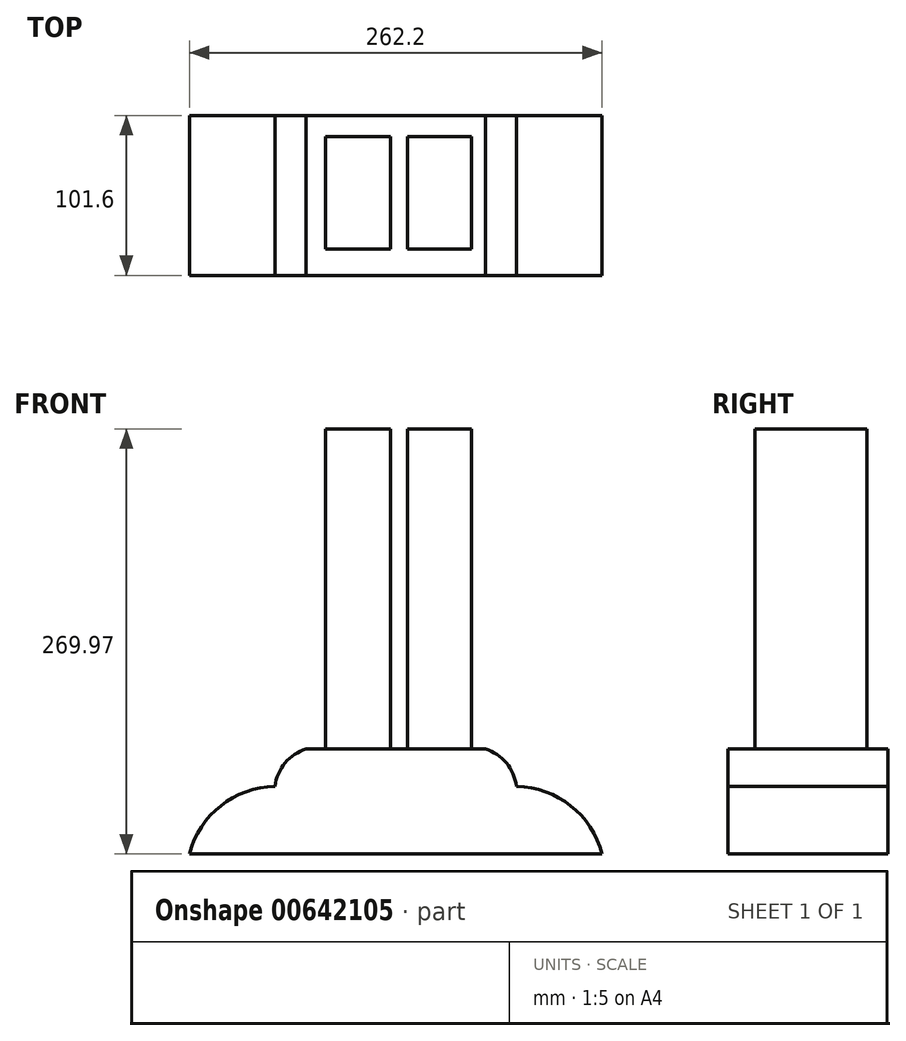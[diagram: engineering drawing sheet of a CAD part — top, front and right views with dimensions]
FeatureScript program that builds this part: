
annotation { "Feature Type Name" : "Feature", "Feature Type Description" : "" }
export const myFeature = defineFeature(function(context is Context, id is Id, definition is map)
    precondition{}
    {
        {
            var Q0;
            Q0=qCreatedBy(makeId("Front.planeOp"),FACE);
            var sketch = newSketch(context, id + "F0", { "sketchPlane" : qUnion([Q0])});
            skLineSegment(sketch, "E0", {"start": v(-122.75, -43.03) * mm, "end": v(131.1, -43.03) * mm});
            skArc(sketch, "E1", {"start": v(131.1, -43.03) * mm, "mid": v(111.1, -12.4) * mm, "end": v(76.7, 0) * mm});
            skArc(sketch, "E2", {"start": v(76.7, 0) * mm, "mid": v(70.24, 14.77) * mm, "end": v(56.84, 23.74) * mm});
            skArc(sketch, "E3.MirrorCS", {"start": v(-76.7, 0) * mm, "mid": v(-70.24, 14.77) * mm, "end": v(-56.84, 23.74) * mm});
            skArc(sketch, "E4.MirrorCS", {"start": v(-131.1, -43.03) * mm, "mid": v(-111.1, -12.4) * mm, "end": v(-76.7, 0) * mm});
            skLineSegment(sketch, "E5", {"start": v(56.84, 23.74) * mm, "end": v(-56.84, 23.74) * mm});
            skLineSegment(sketch, "E6", {"start": v(-122.75, -43.03) * mm, "end": v(-131.1, -43.03) * mm});
            skSolve(sketch);
        }
        {
            var Q0;
            Q0=makeQuery(id+"F0.imprint","IMPRINT",FACE,{"disambiguationData":[TD([[makeQuery(id+"F0.imprint","IMPRINT",EDGE,{"derivedFrom":sQuery(id+"F0.wireOp",EDGE,"E0")}),1.0]])]});
            extrude(context, id + "F1", {"entities" : qUnion([Q0]), "depth" : 101.6 * mm, "offsetDistance" : 25.4 * mm});
        }
        {
            var Q0;
            Q0=makeQuery(id+"F1.opExtrude","SWEPT_FACE",FACE,{"disambiguationData":[OSD([sQuery(id+"F0.wireOp",EDGE,"E5")])]});
            var sketch = newSketch(context, id + "F2", { "sketchPlane" : qUnion([Q0])});
            skLineSegment(sketch, "E7.bottom", {"start": v(-44.51, -13.46) * mm, "end": v(-3.47, -13.46) * mm});
            skLineSegment(sketch, "E7.top", {"start": v(-44.51, -84.71) * mm, "end": v(-3.47, -84.71) * mm});
            skLineSegment(sketch, "E7.left", {"start": v(-44.51, -13.46) * mm, "end": v(-44.51, -84.71) * mm});
            skLineSegment(sketch, "E7.right", {"start": v(-3.47, -13.46) * mm, "end": v(-3.47, -84.71) * mm});
            skLineSegment(sketch, "E8.bottom", {"start": v(7.3, -84.71) * mm, "end": v(48.08, -84.71) * mm});
            skLineSegment(sketch, "E8.top", {"start": v(7.3, -13.46) * mm, "end": v(48.08, -13.46) * mm});
            skLineSegment(sketch, "E8.left", {"start": v(7.3, -84.71) * mm, "end": v(7.3, -13.46) * mm});
            skLineSegment(sketch, "E8.right", {"start": v(48.08, -84.71) * mm, "end": v(48.08, -13.46) * mm});
            skSolve(sketch);
        }
        {
            var Q0;
            Q0=makeQuery(id+"F2.imprint","IMPRINT",FACE,{"disambiguationData":[TD([[makeQuery(id+"F2.imprint","IMPRINT",EDGE,{"derivedFrom":sQuery(id+"F2.wireOp",EDGE,"E7.bottom")}),-1.0]])]});
            var Q1;
            Q1=makeQuery(id+"F2.imprint","IMPRINT",FACE,{"disambiguationData":[TD([[makeQuery(id+"F2.imprint","IMPRINT",EDGE,{"derivedFrom":sQuery(id+"F2.wireOp",EDGE,"E8.bottom")}),1.0]])]});
            extrude(context, id + "F3", {"entities" : qUnion([Q0, Q1]), "operationType" : NewBodyOperationType.ADD, "depth" : 203.2 * mm, "offsetDistance" : 25.4 * mm});
        }
    });
